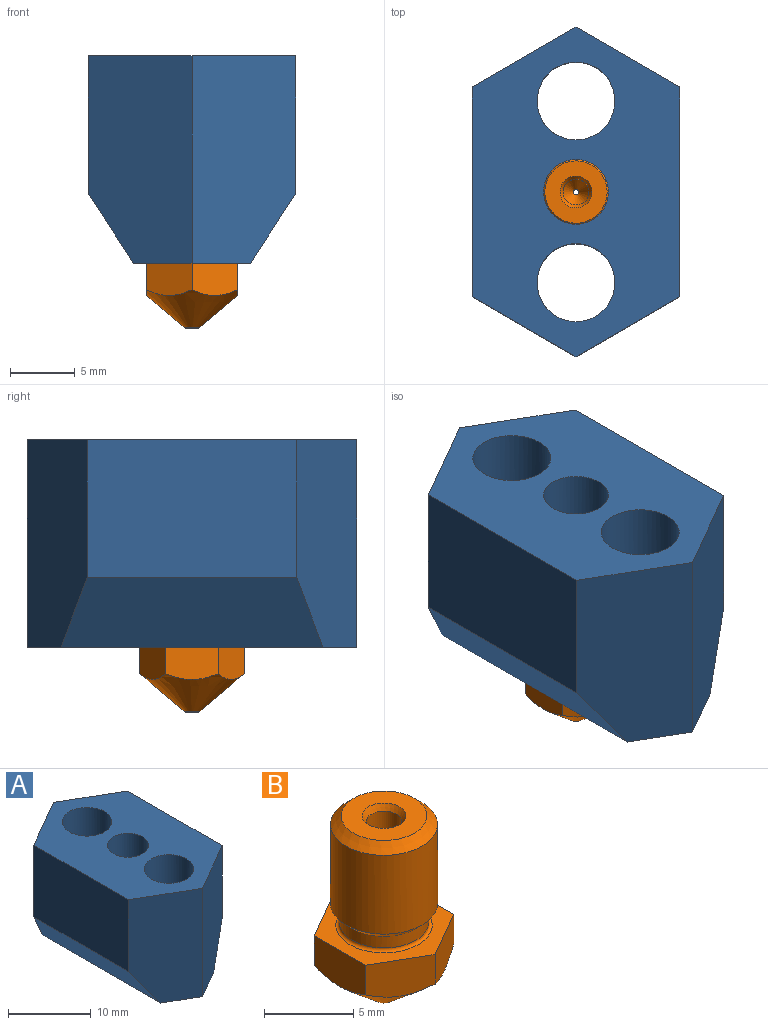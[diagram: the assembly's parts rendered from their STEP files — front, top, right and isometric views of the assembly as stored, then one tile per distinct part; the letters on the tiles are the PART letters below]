
ASSEMBLY  parts=2 mates=1
PART A: 13 faces, bbox 16x25.4x16 mm
  f0: plane 25.4x16mm, normal (0,0,1), area 256.4mm2, adj f1,f2,f4,f5,f7,f8,f9,f11
  f1: plane 16x8mm, normal (0.5,0.87,0), area 136.9mm2, adj f0,f5,f6,f10,f12
  f2: plane 16x8mm, normal (-0.5,-0.87,0), area 136.9mm2, adj f0,f3,f4,f6,f11
  f3: plane 20.21x5.38mm, normal (-0.84,0,-0.54), area 116.8mm2, adj f2,f5,f6,f11
  f4: plane 16x8mm, normal (0.5,-0.87,0), area 136.9mm2, adj f0,f2,f6,f10,f12
  f5: plane 16x8mm, normal (-0.5,0.87,0), area 136.9mm2, adj f0,f1,f3,f6,f11
  f6: plane 25.4x9mm, normal (0,0,-1), area 129.1mm2, adj f1,f2,f3,f4,f5,f7,f8,f9
  f7: cylinder r=2.5mm len=16mm, axis (0,0,-1), area 251.3mm2, adj f0,f6
  f8: cylinder r=3mm len=16mm, axis (0,0,-1), area 301.6mm2, adj f0,f6
  f9: cylinder r=3mm len=16mm, axis (0,0,-1), area 301.6mm2, adj f0,f6
  f10: plane 20.21x5.38mm, normal (0.84,0,-0.54), area 116.8mm2, adj f1,f4,f6,f12
  f11: plane 16.17x10.62mm, normal (-1,0,0), area 171.6mm2, adj f0,f2,f3,f5
  f12: plane 16.17x10.62mm, normal (1,0,0), area 171.6mm2, adj f0,f1,f4,f10
PART B: 20 faces, bbox 8.1x8.1x12.5 mm
  f0: plane 8.08x7mm, normal (0,0,1), area 19.5mm2, adj f10,f11,f12,f13,f14,f15,f18
  f1: cone r=0.5mm half-angle=50deg, axis (0,0,1), area 54.1mm2, adj f10,f11,f12,f13,f14,f15,f19
  f2: cylinder r=2.5mm len=5mm, axis (0,0,-1), area 12.6mm2, adj f17,f18
  f3: cylinder r=3mm len=6mm, axis (0,0,-1), area 101.8mm2, adj f16,f17
  f4: plane 4.8x4.8mm, normal (0,0,1), area 13.3mm2, adj f5,f16
  f5: cone r=1mm half-angle=30deg, axis (0,0,1), area 3.2mm2, adj f4,f6
  f6: cylinder r=1mm len=10.11mm, axis (0,0,-1), area 63.6mm2, adj f5,f7
  f7: cone r=0.2mm half-angle=30deg, axis (0,0,1), area 6mm2, adj f6,f8
  f8: cylinder r=0.2mm len=0.6mm, axis (0,0,-1), area 0.8mm2, adj f7,f9
  f9: plane 0.85x0.85mm, normal (0,0,-1), area 0.4mm2, adj f8,f19
  f10: plane 4.05x2.49mm, normal (1,0,0), area 9.4mm2, adj f0,f1,f11,f15
  f11: plane 3.5x2.49mm, normal (0.5,0.87,0), area 9.4mm2, adj f0,f1,f10,f12
  f12: plane 3.5x2.49mm, normal (-0.5,0.87,0), area 9.4mm2, adj f0,f1,f11,f13
  f13: plane 4.05x2.49mm, normal (-1,0,0), area 9.4mm2, adj f0,f1,f12,f14
  f14: plane 3.5x2.49mm, normal (-0.5,-0.87,0), area 9.4mm2, adj f0,f1,f13,f15
  f15: plane 3.5x2.49mm, normal (0.5,-0.87,0), area 9.4mm2, adj f0,f1,f10,f14
  f16: cone r=3mm half-angle=45deg, axis (0,0,-1), area 14.4mm2, adj f3,f4
  f17: cone r=2.5mm half-angle=45deg, axis (0,0,1), area 12.2mm2, adj f2,f3
  f18: torus R=2.7mm, axis (0,0,1), area 5.1mm2, adj f0,f2
  f19: torus R=0.43mm, axis (0,0,-1), area 0.4mm2, adj f1,f9
PLACE A t=(0,0,-16)mm
PLACE B t=(0,0,-21)mm
MATE fastened B.f1 <-> A.f7  axis (0,0,1) through (0,0,-16)mm
